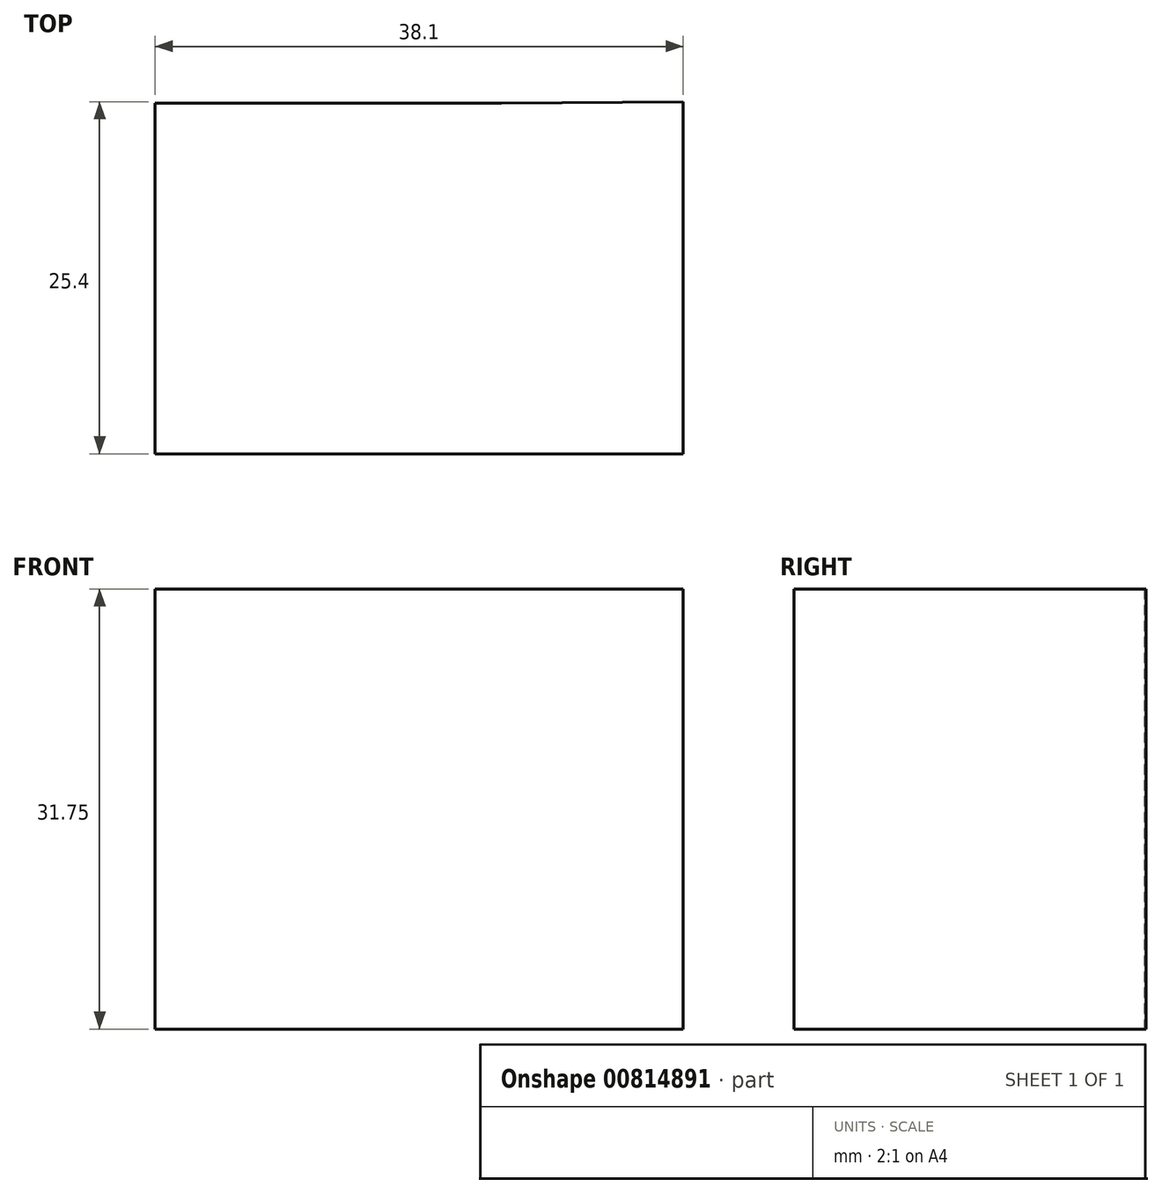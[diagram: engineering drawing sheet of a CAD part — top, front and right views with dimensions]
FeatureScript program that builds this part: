
annotation { "Feature Type Name" : "Feature", "Feature Type Description" : "" }
export const myFeature = defineFeature(function(context is Context, id is Id, definition is map)
    precondition{}
    {
        {
            var Q0;
            Q0=qCreatedBy(makeId("Top.planeOp"),FACE);
            var sketch = newSketch(context, id + "F0", { "sketchPlane" : qUnion([Q0])});
            skLineSegment(sketch, "E0", {"start": v(0, 0) * mm, "end": v(38.1, 0) * mm});
            skLineSegment(sketch, "E1", {"start": v(38.1, 0) * mm, "end": v(38.1, 25.4) * mm});
            skLineSegment(sketch, "E2", {"start": v(24.96, 25.27) * mm, "end": v(0, 25.27) * mm});
            skLineSegment(sketch, "E3", {"start": v(0, 25.27) * mm, "end": v(0, 0) * mm});
            skLineSegment(sketch, "E4", {"start": v(24.96, 25.27) * mm, "end": v(38.1, 25.4) * mm});
            skSolve(sketch);
        }
        {
            var Q0;
            Q0 = qSketchRegion(id + "F0", true);
            extrude(context, id + "F1", {"entities" : qUnion([Q0]), "depth" : 31.75 * mm, "offsetDistance" : 25.4 * mm});
        }
    });
